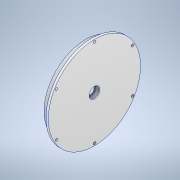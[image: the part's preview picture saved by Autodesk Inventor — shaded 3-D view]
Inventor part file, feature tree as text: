
AUTODESK INVENTOR PART (.ipt)
format: ipt  version: 2020 (Build 240168000, 168)  size: 184,832 bytes
history: native  units: mm
features: sketch x2, revolve x1, chamfer x1, hole x1, pattern_circular x1, projected_geometry x1
ambient origin geometry x8: Origin, YZ Plane, XZ Plane, XY Plane, X Axis, Y Axis, Z Axis, Center Point
bodies: Solid1 (feature_tree)
feature tree (7):
  revolve  "Revolution1"  [1 undecoded]
  chamfer  "Chamfer1"  Distance=1.5mm
  hole  "Hole1"  [1 undecoded]
  pattern_circular  "Circular Pattern1"  [2 undecoded]
  sketch  "Sketch1"  dims[d6=69.57767mm d7=8.5mm]
  sketch  "Sketch2"  dims[d11=90.0deg d15=1.5mm d17=6.0mm d18=1.625mm d19=1.0mm d20=2.0mm d21=45.0deg d22=7.0mm d23=1.0mm d24=2.0mm d25=64.0mm d26=4.0mm d27=15.0mm d29=4.0mm d30=8.0mm d31=4.0mm d32=4.0mm d33=4.5mm d34=6.0mm d35=9.4mm d36=2.0mm d37=90.0deg d38=8.0mm d39=20.594885mm d40=60.0mm d41=360.0deg]
  projected_geometry  "Projected Loop1"
note: 4 required parameter values undecoded (feature->parameter linkage not recoverable at this tier; creation-order binding heuristic only, values carry confidence <= 0.55)